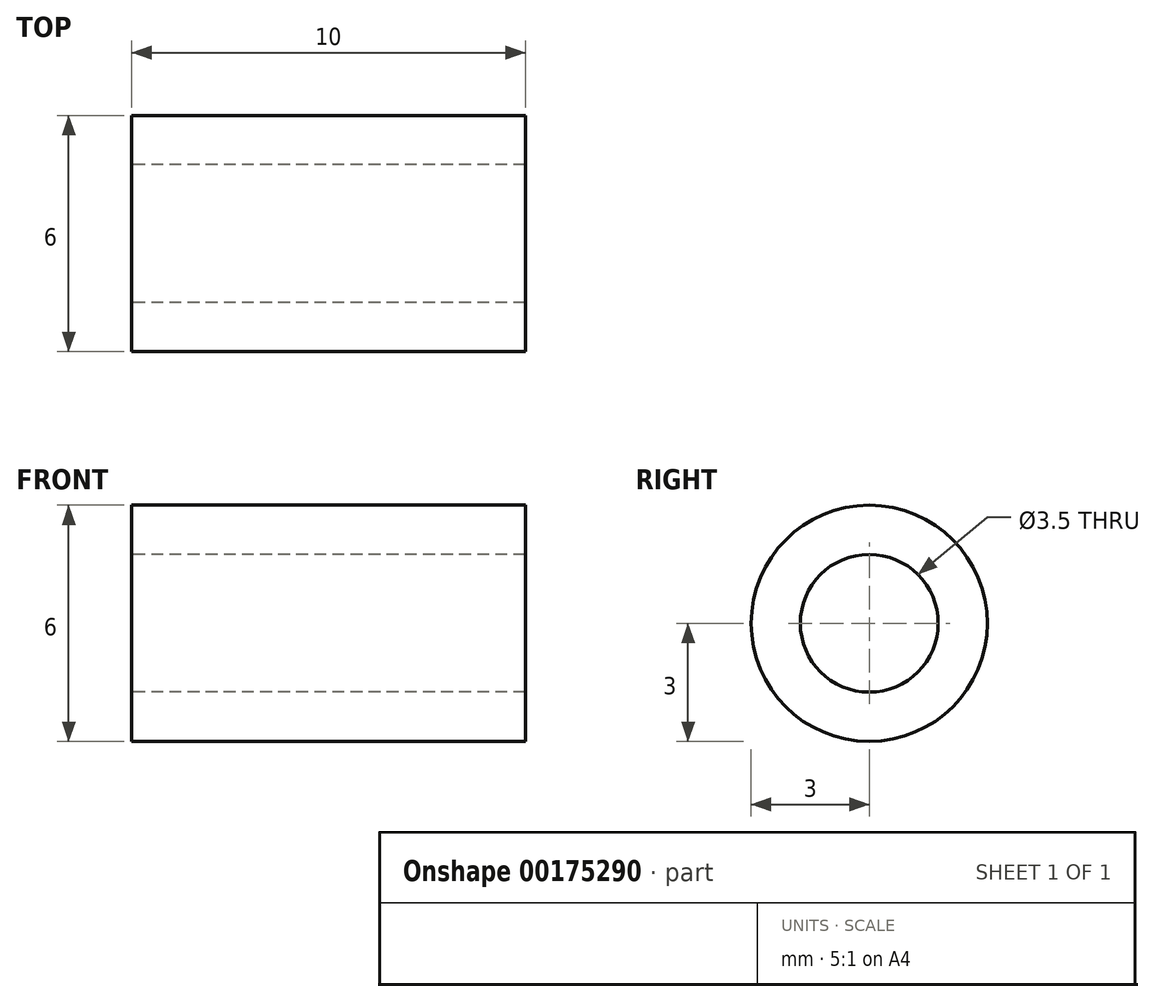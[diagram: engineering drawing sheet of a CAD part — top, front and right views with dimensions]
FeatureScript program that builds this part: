
annotation { "Feature Type Name" : "Feature", "Feature Type Description" : "" }
export const myFeature = defineFeature(function(context is Context, id is Id, definition is map)
    precondition{}
    {
        {
            var Q0;
            Q0=qCreatedBy(makeId("Right.planeOp"),FACE);
            var sketch = newSketch(context, id + "F0", { "sketchPlane" : qUnion([Q0])});
            skCircle(sketch, "E0", {"center": v(0, 0) * mm, "radius": 3 * mm});
            skCircle(sketch, "E1", {"center": v(0, 0) * mm, "radius": 1.75 * mm});
            skSolve(sketch);
        }
        {
            var Q0;
            Q0=qSketchRegion(id+"F0",true);
            extrude(context, id + "F1", {"entities" : qUnion([Q0]), "depth" : 10 * mm});
        }
    });
